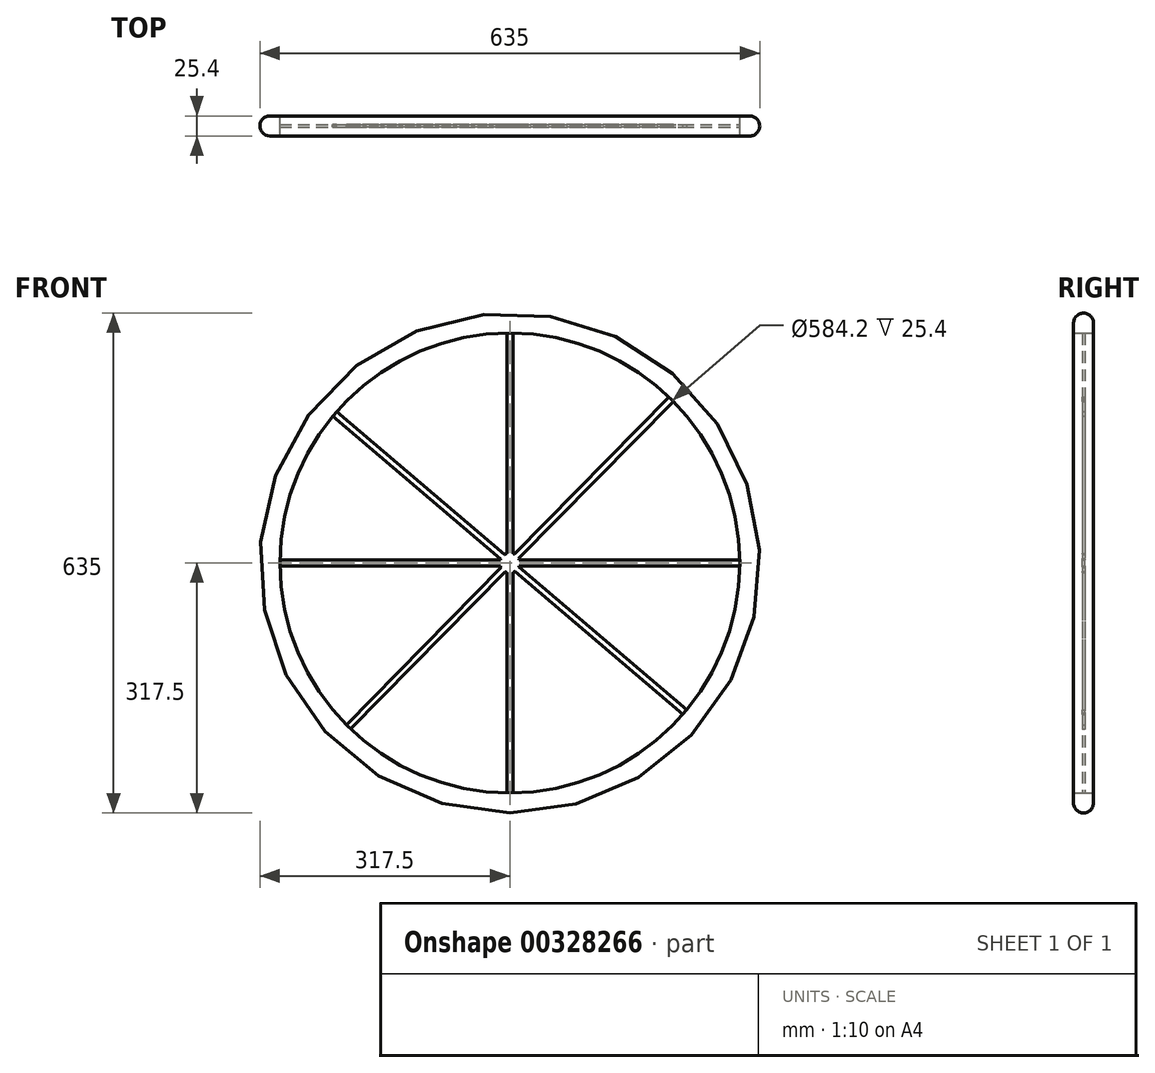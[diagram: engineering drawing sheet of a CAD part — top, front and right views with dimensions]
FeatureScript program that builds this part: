
annotation { "Feature Type Name" : "Feature", "Feature Type Description" : "" }
export const myFeature = defineFeature(function(context is Context, id is Id, definition is map)
    precondition{}
    {
        {
            var Q0;
            Q0=qCreatedBy(makeId("Front.planeOp"),FACE);
            var sketch = newSketch(context, id + "F0", { "sketchPlane" : qUnion([Q0])});
            skCircle(sketch, "E0", {"center": v(0, 0) * mm, "radius": 12.7 * mm});
            skCircle(sketch, "E1", {"center": v(0, 0) * mm, "radius": 317.5 * mm});
            skCircle(sketch, "E2", {"center": v(0, 0) * mm, "radius": 292.1 * mm});
            skLineSegment(sketch, "E3", {"start": v(-3.8, 292.08) * mm, "end": v(-3.8, 12.12) * mm});
            skLineSegment(sketch, "E4", {"start": v(3.8, 292.08) * mm, "end": v(3.8, 12.12) * mm});
            skLineSegment(sketch, "E5", {"start": v(-292.08, 3.81) * mm, "end": v(-12.12, 3.81) * mm});
            skLineSegment(sketch, "E6", {"start": v(-292.08, -3.81) * mm, "end": v(-12.12, -3.81) * mm});
            skLineSegment(sketch, "E7", {"start": v(202.2, 210.8) * mm, "end": v(5.79, 11.3) * mm});
            skLineSegment(sketch, "E8", {"start": v(207.64, 205.45) * mm, "end": v(11.21, 5.96) * mm});
            skLineSegment(sketch, "E9", {"start": v(-219.88, 192.29) * mm, "end": v(-6.75, 10.76) * mm});
            skLineSegment(sketch, "E10", {"start": v(-224.82, 186.49) * mm, "end": v(-11.7, 4.96) * mm});
            skLineSegment(sketch, "E11.trimOffspring", {"start": v(11.7, -4.96) * mm, "end": v(224.82, -186.49) * mm});
            skLineSegment(sketch, "E12.trimOffspring", {"start": v(3.81, -12.12) * mm, "end": v(3.81, -300.4) * mm});
            skLineSegment(sketch, "E13.trimOffspring", {"start": v(12.12, 3.81) * mm, "end": v(292.08, 3.81) * mm});
            skLineSegment(sketch, "E14.trimOffspring", {"start": v(-11.21, -5.96) * mm, "end": v(-207.64, -205.45) * mm});
            skLineSegment(sketch, "E15.trimOffspring", {"start": v(-5.79, -11.3) * mm, "end": v(-202.2, -210.8) * mm});
            skLineSegment(sketch, "E16.trimOffspring", {"start": v(-3.8, -12.12) * mm, "end": v(-3.8, -292.08) * mm});
            skLineSegment(sketch, "E17.trimOffspring", {"start": v(12.12, -3.81) * mm, "end": v(292.08, -3.81) * mm});
            skLineSegment(sketch, "E18.trimOffspring", {"start": v(6.75, -10.76) * mm, "end": v(219.88, -192.29) * mm});
            skSolve(sketch);
        }
        {
            var Q0;
            Q0=makeQuery(id+"F0.imprint","IMPRINT",FACE,{"disambiguationData":[TD([[makeQuery(id+"F0.imprint","IMPRINT",EDGE,{"derivedFrom":sQuery(id+"F0.wireOp",EDGE,"E1")}),1.0]])]});
            extrude(context, id + "F1", {"entities" : qUnion([Q0]), "endBound" : BoundingType.SYMMETRIC, "depth" : 25.4 * mm});
        }
        {
            var Q0;
            {var subQ0=sQuery(id+"F0.wireOp",EDGE,"E3");Q0=makeQuery(id+"F0.imprint","IMPRINT",FACE,{"disambiguationData":[TD([[makeQuery(id+"F0.imprint","IMPRINT",EDGE,{"derivedFrom":subQ0}),1.0]])]});}
            var Q1;
            {var subQ0=sQuery(id+"F0.wireOp",EDGE,"E9");Q1=makeQuery(id+"F0.imprint","IMPRINT",FACE,{"disambiguationData":[TD([[makeQuery(id+"F0.imprint","IMPRINT",EDGE,{"derivedFrom":subQ0}),-1.0]])]});}
            var Q2;
            {var subQ0=sQuery(id+"F0.wireOp",EDGE,"E7");Q2=makeQuery(id+"F0.imprint","IMPRINT",FACE,{"disambiguationData":[TD([[makeQuery(id+"F0.imprint","IMPRINT",EDGE,{"derivedFrom":subQ0}),1.0]])]});}
            var Q3;
            {var subQ0=sQuery(id+"F0.wireOp",EDGE,"E13.trimOffspring");Q3=makeQuery(id+"F0.imprint","IMPRINT",FACE,{"disambiguationData":[TD([[makeQuery(id+"F0.imprint","IMPRINT",EDGE,{"derivedFrom":subQ0}),-1.0]])]});}
            var Q4;
            {var subQ0=sQuery(id+"F0.wireOp",EDGE,"E11.trimOffspring");Q4=makeQuery(id+"F0.imprint","IMPRINT",FACE,{"disambiguationData":[TD([[makeQuery(id+"F0.imprint","IMPRINT",EDGE,{"derivedFrom":subQ0}),-1.0]])]});}
            var Q5;
            {var subQ3=sQuery(id+"F0.wireOp",EDGE,"E16.trimOffspring");Q5=makeQuery(id+"F0.imprint","IMPRINT",FACE,{"disambiguationData":[TD([[makeQuery(id+"F0.imprint","IMPRINT",EDGE,{"derivedFrom":subQ3}),1.0]])]});}
            var Q6;
            {var subQ0=sQuery(id+"F0.wireOp",EDGE,"E5");Q6=makeQuery(id+"F0.imprint","IMPRINT",FACE,{"disambiguationData":[TD([[makeQuery(id+"F0.imprint","IMPRINT",EDGE,{"derivedFrom":subQ0}),-1.0]])]});}
            var Q7;
            {var subQ0=sQuery(id+"F0.wireOp",EDGE,"E14.trimOffspring");Q7=makeQuery(id+"F0.imprint","IMPRINT",FACE,{"disambiguationData":[TD([[makeQuery(id+"F0.imprint","IMPRINT",EDGE,{"derivedFrom":subQ0}),1.0]])]});}
            var Q8;
            {var subQ0=sQuery(id+"F0.wireOp",EDGE,"E0");var subQ8=makeQuery(id+"F0.imprint","INTERSECT",VERTEX,{"derivedFrom":[subQ0,sQuery(id+"F0.wireOp",EDGE,"E8")]});Q8=makeQuery(id+"F0.imprint","IMPRINT",FACE,{"disambiguationData":[TD([[makeQuery(id+"F0.imprint","IMPRINT",EDGE,{"disambiguationData":[TD([[subQ8,1.0]])],"derivedFrom":subQ0}),1.0]])]});}
            extrude(context, id + "F2", {"entities" : qUnion([Q0, Q1, Q2, Q3, Q4, Q5, Q6, Q7, Q8]), "operationType" : NewBodyOperationType.ADD, "endBound" : BoundingType.SYMMETRIC, "depth" : 3.17 * mm});
        }
        {
            var Q0;
            Q0=makeQuery(id+"F1.opExtrude","CAP_EDGE",EDGE,{"disambiguationData":[OSD([sQuery(id+"F0.wireOp",EDGE,"E1")])],"isStart":false});
            var Q1;
            Q1=makeQuery(id+"F1.opExtrude","CAP_EDGE",EDGE,{"disambiguationData":[OSD([sQuery(id+"F0.wireOp",EDGE,"E1")])],"isStart":true});
            fillet(context, id + "F3", {"entities" : qUnion([Q0, Q1]), "radius" : 12.7 * mm, "tangentPropagation" : true, "allowEdgeOverflow" : false});
        }
    });
